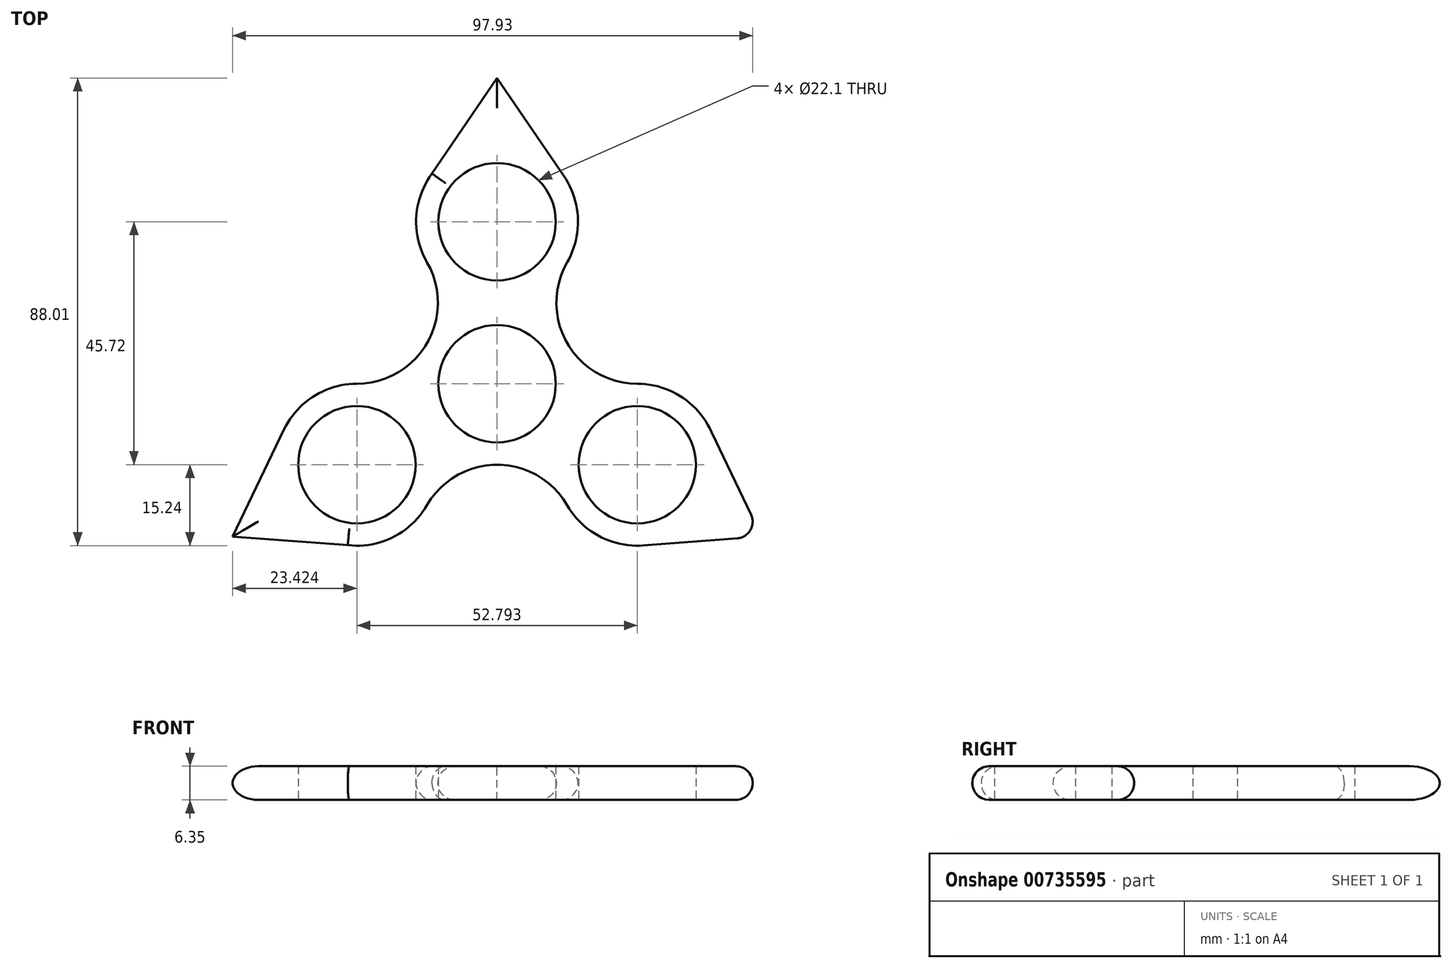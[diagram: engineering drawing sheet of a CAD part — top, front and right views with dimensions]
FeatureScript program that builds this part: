
annotation { "Feature Type Name" : "Feature", "Feature Type Description" : "" }
export const myFeature = defineFeature(function(context is Context, id is Id, definition is map)
    precondition{}
    {
        {
            var Q0;
            Q0=qCreatedBy(makeId("Top.planeOp"),FACE);
            var sketch = newSketch(context, id + "F0", { "sketchPlane" : qUnion([Q0])});
            skCircle(sketch, "E0", {"center": v(0, 0) * mm, "radius": 11.05 * mm});
            skLineSegment(sketch, "E1", {"start": v(0, 0) * mm, "end": v(0, 30.48) * mm});
            skArc(sketch, "E2", {"start": v(-12.25, 39.54) * mm, "mid": v(-15.22, 31.34) * mm, "end": v(-13.2, 22.86) * mm});
            skArc(sketch, "E3.1.0", {"start": v(-28.12, -30.38) * mm, "mid": v(-19.54, -28.85) * mm, "end": v(-13.2, -22.86) * mm});
            skArc(sketch, "E3.2.0", {"start": v(13.2, -22.86) * mm, "mid": v(19.28, -28.71) * mm, "end": v(27.54, -30.44) * mm});
            skLineSegment(sketch, "E4", {"start": v(0, 0) * mm, "end": v(-26.4, 15.24) * mm});
            skArc(sketch, "E5", {"start": v(-26.4, 0) * mm, "mid": v(-13.2, 7.62) * mm, "end": v(-13.2, 22.86) * mm});
            skArc(sketch, "E6.1.0", {"start": v(13.2, -22.86) * mm, "mid": v(0, -15.24) * mm, "end": v(-13.2, -22.86) * mm});
            skArc(sketch, "E6.2.0", {"start": v(13.2, 22.86) * mm, "mid": v(13.2, 7.62) * mm, "end": v(26.4, 0) * mm});
            skLineSegment(sketch, "E7", {"start": v(-12.25, 39.54) * mm, "end": v(0, 57.53) * mm});
            skLineSegment(sketch, "E8", {"start": v(0, 57.53) * mm, "end": v(12.6, 39.07) * mm});
            skLineSegment(sketch, "E9.1.0", {"start": v(-49.82, -28.76) * mm, "end": v(-40.13, -8.63) * mm});
            skLineSegment(sketch, "E9.2.0", {"start": v(49.82, -28.76) * mm, "end": v(27.54, -30.44) * mm});
            skLineSegment(sketch, "E10.1.0", {"start": v(-28.12, -30.38) * mm, "end": v(-49.82, -28.76) * mm});
            skLineSegment(sketch, "E10.2.0", {"start": v(40.37, -9.16) * mm, "end": v(49.82, -28.76) * mm});
            skCircle(sketch, "E11", {"center": v(0, 30.48) * mm, "radius": 11.05 * mm});
            skCircle(sketch, "E12.1.0", {"center": v(-26.4, -15.24) * mm, "radius": 11.05 * mm});
            skCircle(sketch, "E12.2.0", {"center": v(26.4, -15.24) * mm, "radius": 11.05 * mm});
            skArc(sketch, "E13.trimOffspring", {"start": v(13.2, 22.86) * mm, "mid": v(15.23, 31.05) * mm, "end": v(12.6, 39.07) * mm});
            skArc(sketch, "E14.trimOffspring", {"start": v(-26.4, 0) * mm, "mid": v(-34.5, -2.34) * mm, "end": v(-40.13, -8.63) * mm});
            skArc(sketch, "E15.trimOffspring", {"start": v(40.37, -9.16) * mm, "mid": v(34.75, -2.5) * mm, "end": v(26.4, 0) * mm});
            skSolve(sketch);
        }
        {
            var Q0;
            Q0 = qSketchRegion(id + "F0", true);
            extrude(context, id + "F1", {"entities" : qUnion([Q0]), "depth" : 6.35 * mm, "offsetDistance" : 25.4 * mm});
        }
        {
            var Q0;
            Q0=makeQuery(id+"F1.opExtrude","CAP_EDGE",EDGE,{"disambiguationData":[OSD([sQuery(id+"F0.wireOp",EDGE,"E7")])],"isStart":false});
            var Q1;
            Q1=makeQuery(id+"F1.opExtrude","CAP_EDGE",EDGE,{"disambiguationData":[OSD([sQuery(id+"F0.wireOp",EDGE,"E8")])],"isStart":false});
            var Q2;
            Q2=makeQuery(id+"F1.opExtrude","CAP_EDGE",EDGE,{"disambiguationData":[OSD([sQuery(id+"F0.wireOp",EDGE,"E13.trimOffspring")])],"isStart":false});
            var Q3;
            Q3=makeQuery(id+"F1.opExtrude","CAP_EDGE",EDGE,{"disambiguationData":[OSD([sQuery(id+"F0.wireOp",EDGE,"E6.2.0")])],"isStart":false});
            var Q4;
            Q4=makeQuery(id+"F1.opExtrude","CAP_EDGE",EDGE,{"disambiguationData":[OSD([sQuery(id+"F0.wireOp",EDGE,"E15.trimOffspring")])],"isStart":false});
            var Q5;
            Q5=makeQuery(id+"F1.opExtrude","CAP_EDGE",EDGE,{"disambiguationData":[OSD([sQuery(id+"F0.wireOp",EDGE,"E10.2.0")])],"isStart":false});
            var Q6;
            Q6=makeQuery(id+"F1.opExtrude","CAP_EDGE",EDGE,{"disambiguationData":[OSD([sQuery(id+"F0.wireOp",EDGE,"E9.2.0")])],"isStart":false});
            var Q7;
            Q7=makeQuery(id+"F1.opExtrude","CAP_EDGE",EDGE,{"disambiguationData":[OSD([sQuery(id+"F0.wireOp",EDGE,"E3.2.0")])],"isStart":false});
            var Q8;
            Q8=makeQuery(id+"F1.opExtrude","CAP_EDGE",EDGE,{"disambiguationData":[OSD([sQuery(id+"F0.wireOp",EDGE,"E6.1.0")])],"isStart":false});
            var Q9;
            Q9=makeQuery(id+"F1.opExtrude","CAP_EDGE",EDGE,{"disambiguationData":[OSD([sQuery(id+"F0.wireOp",EDGE,"E3.1.0")])],"isStart":false});
            var Q10;
            Q10=makeQuery(id+"F1.opExtrude","CAP_EDGE",EDGE,{"disambiguationData":[OSD([sQuery(id+"F0.wireOp",EDGE,"E10.1.0")])],"isStart":false});
            var Q11;
            Q11=makeQuery(id+"F1.opExtrude","CAP_EDGE",EDGE,{"disambiguationData":[OSD([sQuery(id+"F0.wireOp",EDGE,"E9.1.0")])],"isStart":false});
            var Q12;
            Q12=makeQuery(id+"F1.opExtrude","CAP_EDGE",EDGE,{"disambiguationData":[OSD([sQuery(id+"F0.wireOp",EDGE,"E14.trimOffspring")])],"isStart":false});
            var Q13;
            Q13=makeQuery(id+"F1.opExtrude","CAP_EDGE",EDGE,{"disambiguationData":[OSD([sQuery(id+"F0.wireOp",EDGE,"E5")])],"isStart":false});
            var Q14;
            Q14=makeQuery(id+"F1.opExtrude","CAP_EDGE",EDGE,{"disambiguationData":[OSD([sQuery(id+"F0.wireOp",EDGE,"E2")])],"isStart":false});
            var Q15;
            Q15=makeQuery(id+"F1.opExtrude","CAP_EDGE",EDGE,{"disambiguationData":[OSD([sQuery(id+"F0.wireOp",EDGE,"E2")])],"isStart":true});
            var Q16;
            Q16=makeQuery(id+"F1.opExtrude","CAP_EDGE",EDGE,{"disambiguationData":[OSD([sQuery(id+"F0.wireOp",EDGE,"E8")])],"isStart":true});
            var Q17;
            Q17=makeQuery(id+"F1.opExtrude","CAP_EDGE",EDGE,{"disambiguationData":[OSD([sQuery(id+"F0.wireOp",EDGE,"E6.2.0")])],"isStart":true});
            var Q18;
            Q18=makeQuery(id+"F1.opExtrude","CAP_EDGE",EDGE,{"disambiguationData":[OSD([sQuery(id+"F0.wireOp",EDGE,"E9.2.0")])],"isStart":true});
            var Q19;
            Q19=makeQuery(id+"F1.opExtrude","SWEPT_FACE",FACE,{"disambiguationData":[OSD([sQuery(id+"F0.wireOp",EDGE,"E13.trimOffspring")])]});
            var Q20;
            Q20=makeQuery(id+"F1.opExtrude","SWEPT_FACE",FACE,{"disambiguationData":[OSD([sQuery(id+"F0.wireOp",EDGE,"E15.trimOffspring")])]});
            var Q21;
            Q21=makeQuery(id+"F1.opExtrude","SWEPT_FACE",FACE,{"disambiguationData":[OSD([sQuery(id+"F0.wireOp",EDGE,"E10.2.0")])]});
            var Q22;
            Q22=makeQuery(id+"F1.opExtrude","CAP_EDGE",EDGE,{"disambiguationData":[OSD([sQuery(id+"F0.wireOp",EDGE,"E5")])],"isStart":true});
            fillet(context, id + "F2", {"entities" : qUnion([Q0, Q1, Q2, Q3, Q4, Q5, Q6, Q7, Q8, Q9, Q10, Q11, Q12, Q13, Q14, Q15, Q16, Q17, Q18, Q19, Q20, Q21, Q22]), "radius" : 3.17 * mm, "tangentPropagation" : true, "allowEdgeOverflow" : false});
        }
    });
